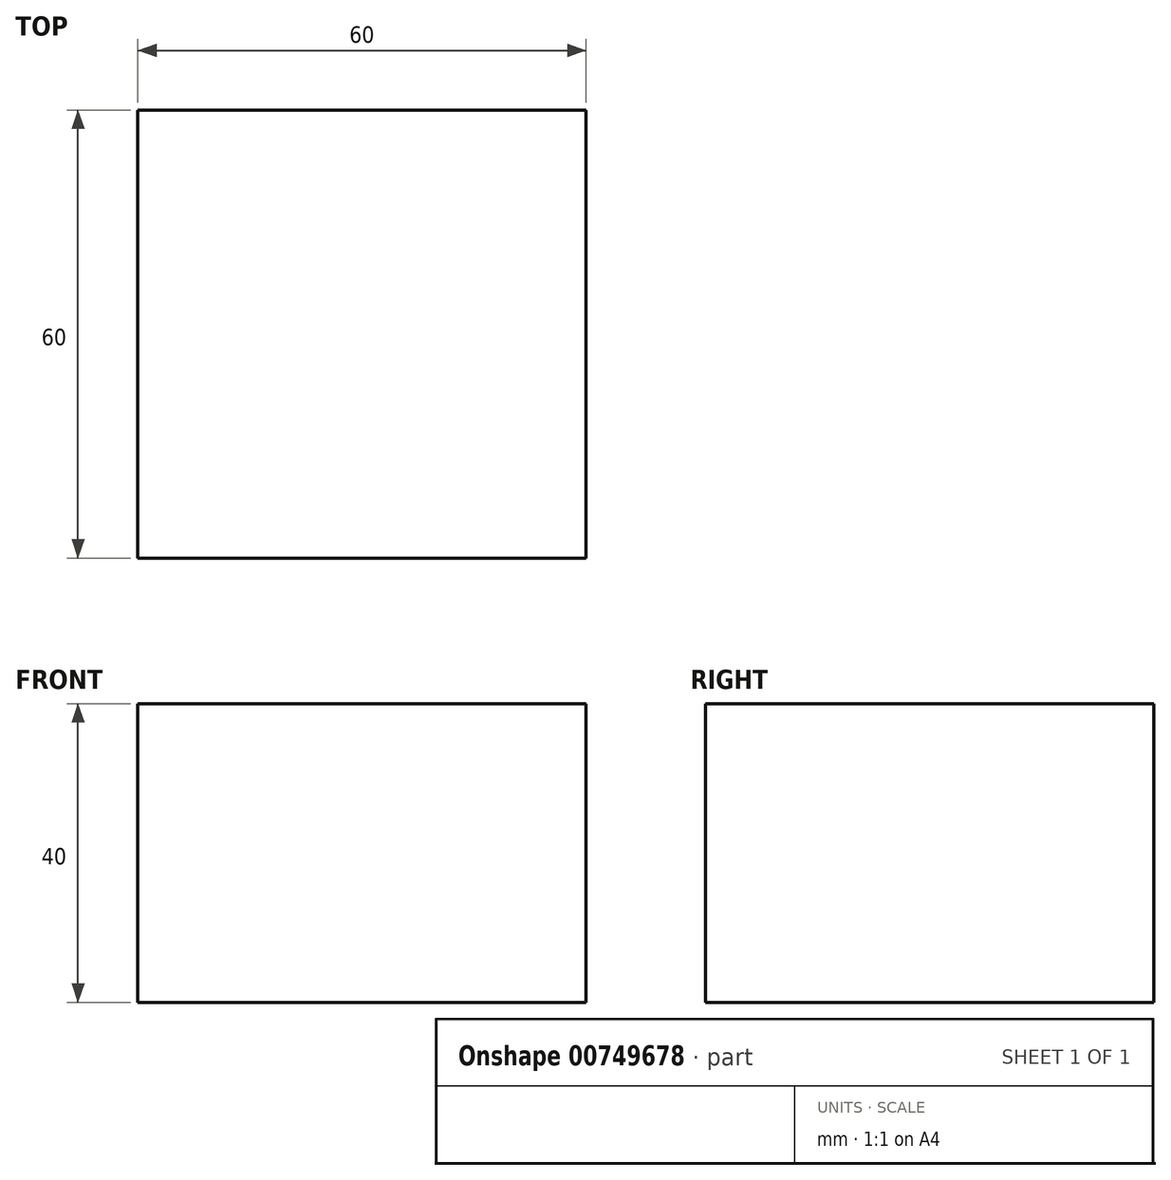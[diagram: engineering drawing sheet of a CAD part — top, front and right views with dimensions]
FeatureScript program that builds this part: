
annotation { "Feature Type Name" : "Feature", "Feature Type Description" : "" }
export const myFeature = defineFeature(function(context is Context, id is Id, definition is map)
    precondition{}
    {
        {
            var Q0;
            Q0=qCreatedBy(makeId("Front.planeOp"),FACE);
            var sketch = newSketch(context, id + "F0", { "sketchPlane" : qUnion([Q0])});
            skLineSegment(sketch, "E0.bottom", {"start": v(0, 0) * mm, "end": v(60, 0) * mm});
            skLineSegment(sketch, "E0.top", {"start": v(0, 40) * mm, "end": v(60, 40) * mm});
            skLineSegment(sketch, "E0.left", {"start": v(0, 0) * mm, "end": v(0, 40) * mm});
            skLineSegment(sketch, "E0.right", {"start": v(60, 0) * mm, "end": v(60, 40) * mm});
            skSolve(sketch);
        }
        {
            var Q0;
            Q0 = qSketchRegion(id + "F0", true);
            extrude(context, id + "F1", {"entities" : qUnion([Q0]), "depth" : 60 * mm, "offsetDistance" : 25 * mm});
        }
    });
